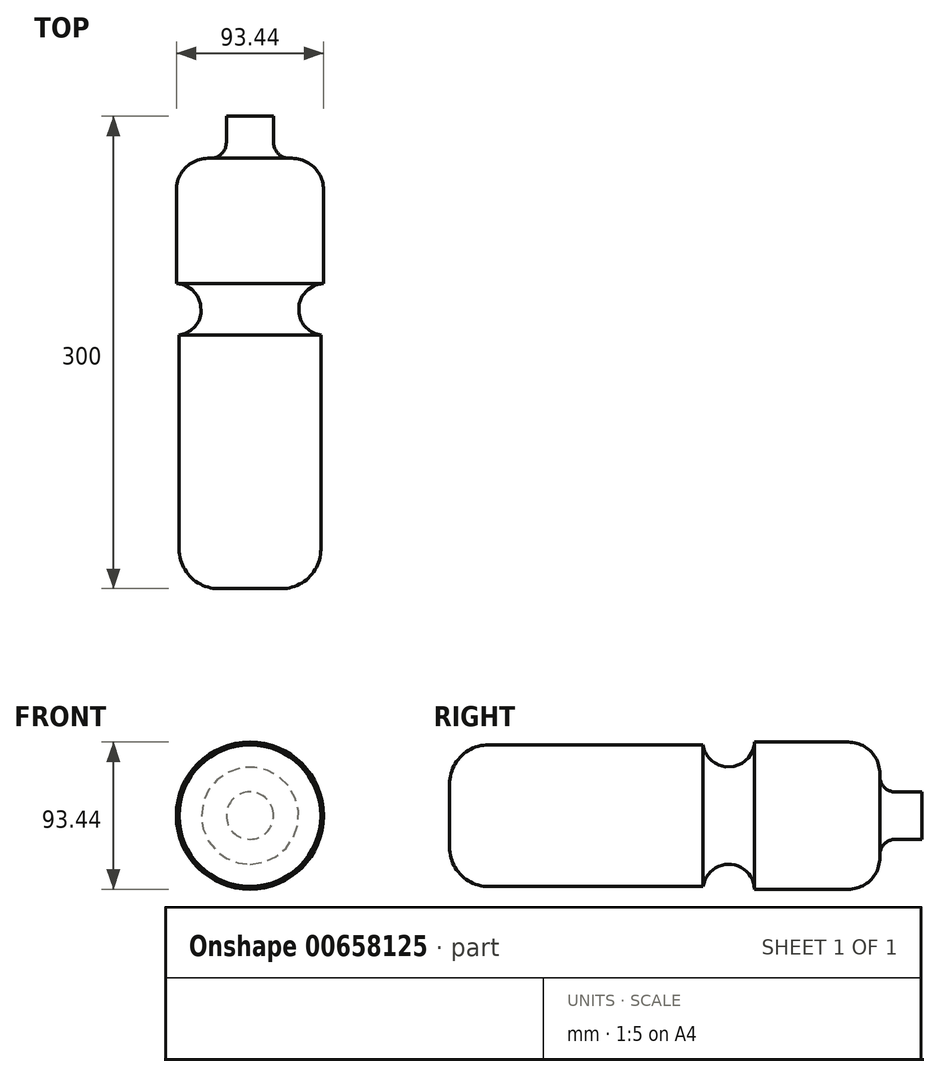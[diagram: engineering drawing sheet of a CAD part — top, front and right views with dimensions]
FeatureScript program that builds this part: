
annotation { "Feature Type Name" : "Feature", "Feature Type Description" : "" }
export const myFeature = defineFeature(function(context is Context, id is Id, definition is map)
    precondition{}
    {
        {
            var Q0;
            Q0=qCreatedBy(makeId("Right.planeOp"),FACE);
            var sketch = newSketch(context, id + "F0", { "sketchPlane" : qUnion([Q0])});
            skLineSegment(sketch, "E0", {"start": v(-204.76, 0) * mm, "end": v(195.24, 0) * mm, "construction": true});
            skLineSegment(sketch, "E1", {"start": v(-204.76, 0) * mm, "end": v(-204.76, 20) * mm});
            skLineSegment(sketch, "E2", {"start": v(-179.76, 45) * mm, "end": v(-43.68, 45) * mm});
            skLineSegment(sketch, "E3", {"start": v(-11.04, 46.72) * mm, "end": v(48.55, 46.72) * mm});
            skLineSegment(sketch, "E4", {"start": v(68.55, 26.72) * mm, "end": v(68.55, 25) * mm});
            skLineSegment(sketch, "E5", {"start": v(78.55, 15) * mm, "end": v(95.24, 15) * mm});
            skLineSegment(sketch, "E6", {"start": v(95.24, 15) * mm, "end": v(95.24, 0) * mm});
            skLineSegment(sketch, "E7", {"start": v(95.24, 0) * mm, "end": v(-204.76, 0) * mm});
            skArc(sketch, "E8", {"start": v(-43.68, 45) * mm, "mid": v(-26.57, 30.9) * mm, "end": v(-11.04, 46.72) * mm});
            skPoint(sketch, "E9.visualSharp", {"position": v(-204.76, 45) * mm});
            skArc(sketch, "E9.filletArc", {"start": v(-179.76, 45) * mm, "mid": v(-197.43, 37.68) * mm, "end": v(-204.76, 20) * mm});
            skPoint(sketch, "E10.visualSharp", {"position": v(68.55, 15) * mm});
            skArc(sketch, "E10.filletArc", {"start": v(68.55, 25) * mm, "mid": v(71.48, 17.93) * mm, "end": v(78.55, 15) * mm});
            skPoint(sketch, "E11.visualSharp", {"position": v(68.55, 46.72) * mm});
            skArc(sketch, "E11.filletArc", {"start": v(68.55, 26.72) * mm, "mid": v(62.7, 40.86) * mm, "end": v(48.55, 46.72) * mm});
            skSolve(sketch);
        }
        {
            var Q0;
            Q0 = qSketchRegion(id + "F0", true);
            var Q1;
            Q1=sQuery(id+"F0.wireOp",EDGE,"E0");
            revolve(context, id + "F1", {"entities" : qUnion([Q0]), "axis" : qUnion([Q1]), "revolveType" : RevolveType.FULL});
        }
    });
